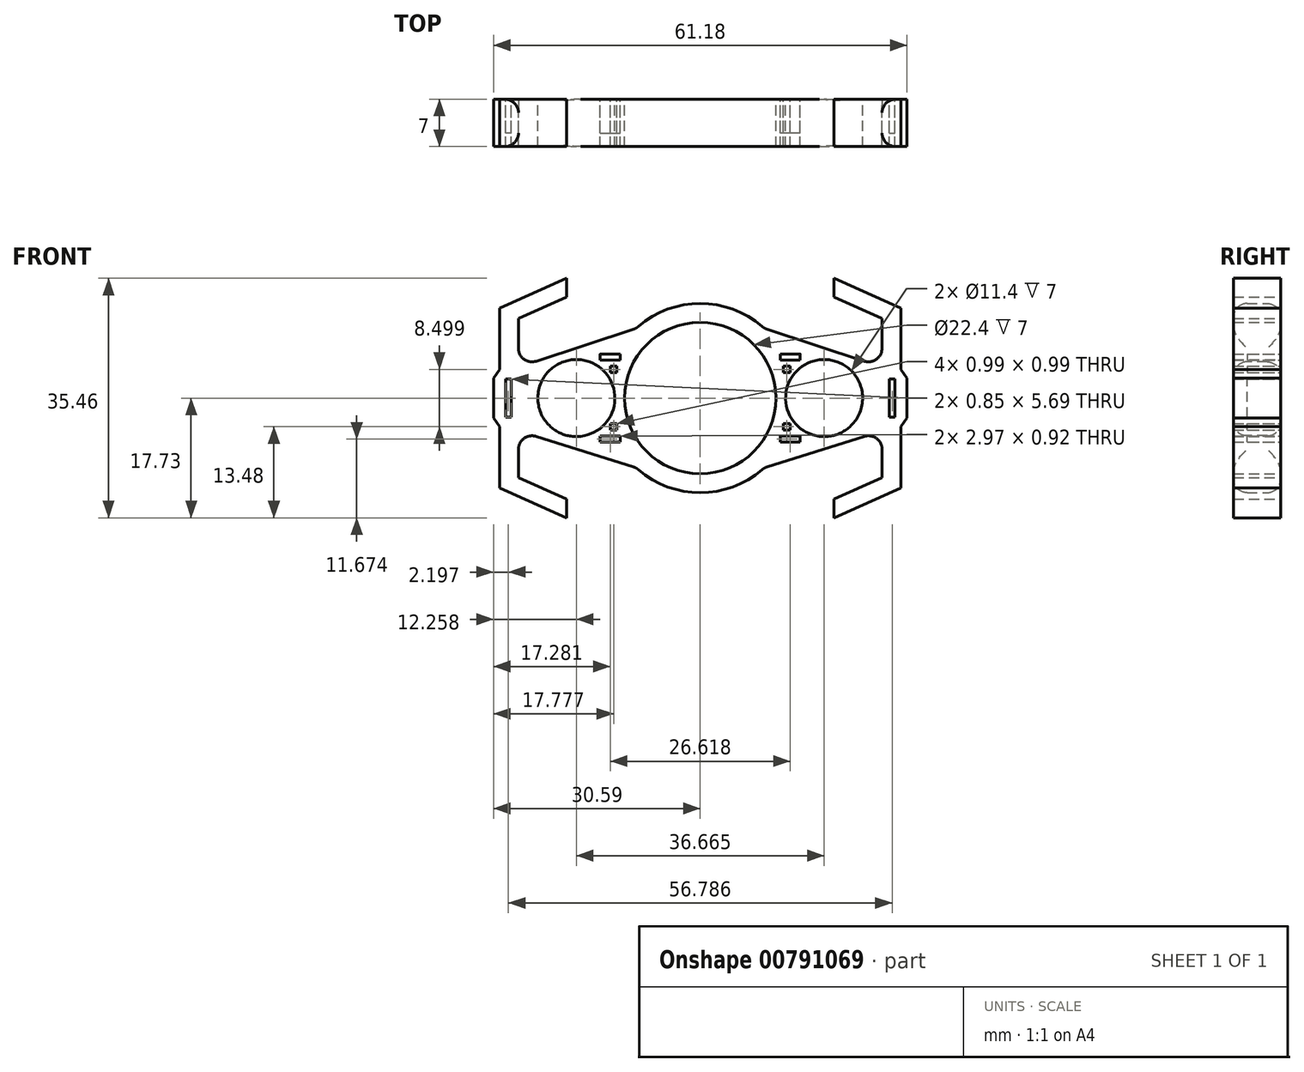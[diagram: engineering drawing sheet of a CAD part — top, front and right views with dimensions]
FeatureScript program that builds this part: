
annotation { "Feature Type Name" : "Feature", "Feature Type Description" : "" }
export const myFeature = defineFeature(function(context is Context, id is Id, definition is map)
    precondition{}
    {
        {
            var Q0;
            Q0=qCreatedBy(makeId("Front.planeOp"),FACE);
            var sketch = newSketch(context, id + "F0", { "sketchPlane" : qUnion([Q0])});
            skCircle(sketch, "E0", {"center": v(0, 0) * mm, "radius": 11.2 * mm});
            skArc(sketch, "E1", {"start": v(-9.46, -10.32) * mm, "mid": v(0, -14) * mm, "end": v(9.46, -10.32) * mm});
            skLineSegment(sketch, "E2", {"start": v(26.9, 4.6) * mm, "end": v(9.46, 10.32) * mm});
            skLineSegment(sketch, "E3", {"start": v(26.9, -4.86) * mm, "end": v(9.46, -10.32) * mm});
            skCircle(sketch, "E4", {"center": v(18.33, 0) * mm, "radius": 5.7 * mm});
            skLineSegment(sketch, "E5.right", {"start": v(29.7, 12.91) * mm, "end": v(29.7, 4.25) * mm});
            skPoint(sketch, "E6.orphan", {"position": v(0, 11.2) * mm});
            skLineSegment(sketch, "E7", {"start": v(29.7, -13.3) * mm, "end": v(19.79, -17.73) * mm});
            skLineSegment(sketch, "E8", {"start": v(19.79, -17.73) * mm, "end": v(19.79, -14.93) * mm});
            skLineSegment(sketch, "E9.top", {"start": v(29.7, -13.3) * mm, "end": v(29.69, -13.3) * mm});
            skLineSegment(sketch, "E9.left", {"start": v(29.7, 13.3) * mm, "end": v(29.7, 12.91) * mm});
            skLineSegment(sketch, "E10", {"start": v(19.79, -14.93) * mm, "end": v(26.9, -11.75) * mm});
            skLineSegment(sketch, "E11.MirrorCS", {"start": v(29.7, -13.3) * mm, "end": v(29.7, -12.91) * mm});
            skLineSegment(sketch, "E12.MirrorCS", {"start": v(29.7, 13.3) * mm, "end": v(19.79, 17.73) * mm});
            skLineSegment(sketch, "E13.MirrorCS", {"start": v(29.7, 13.3) * mm, "end": v(29.69, 13.3) * mm});
            skLineSegment(sketch, "E14.MirrorCS", {"start": v(19.79, 14.93) * mm, "end": v(26.9, 11.75) * mm});
            skLineSegment(sketch, "E15.MirrorCS", {"start": v(19.79, 17.73) * mm, "end": v(19.79, 14.93) * mm});
            skLineSegment(sketch, "E16.trimOffspring", {"start": v(26.9, 11.75) * mm, "end": v(26.9, 4.6) * mm});
            skLineSegment(sketch, "E17.trimOffspring", {"start": v(26.9, -11.75) * mm, "end": v(26.9, -4.86) * mm});
            skLineSegment(sketch, "E18.trimOffspring", {"start": v(29.7, 13.3) * mm, "end": v(29.7, 13.3) * mm});
            skLineSegment(sketch, "E19.trimOffspring", {"start": v(29.7, -13.3) * mm, "end": v(29.7, -13.3) * mm});
            skLineSegment(sketch, "E20", {"start": v(29.7, 4.25) * mm, "end": v(30.6, 2.96) * mm});
            skLineSegment(sketch, "E21", {"start": v(30.6, 2.96) * mm, "end": v(30.6, 0) * mm});
            skLineSegment(sketch, "E22.MirrorCS", {"start": v(30.6, -2.96) * mm, "end": v(30.6, 0) * mm});
            skLineSegment(sketch, "E23.MirrorCS", {"start": v(29.7, -4.25) * mm, "end": v(30.6, -2.96) * mm});
            skLineSegment(sketch, "E24.trimOffspring", {"start": v(29.7, -4.25) * mm, "end": v(29.7, -13.3) * mm});
            skLineSegment(sketch, "E25.MirrorCS", {"start": v(-29.7, -13.3) * mm, "end": v(-29.69, -13.3) * mm});
            skLineSegment(sketch, "E26.MirrorCS", {"start": v(-29.7, -13.3) * mm, "end": v(-29.7, -12.91) * mm});
            skLineSegment(sketch, "E27.MirrorCS", {"start": v(-29.7, -13.3) * mm, "end": v(-29.7, -13.3) * mm});
            skLineSegment(sketch, "E28.MirrorCS", {"start": v(-29.7, 13.3) * mm, "end": v(-29.7, 13.3) * mm});
            skLineSegment(sketch, "E29.MirrorCS", {"start": v(-29.7, 13.3) * mm, "end": v(-29.69, 13.3) * mm});
            skLineSegment(sketch, "E30.MirrorCS", {"start": v(-29.7, 13.3) * mm, "end": v(-29.7, 12.91) * mm});
            skLineSegment(sketch, "E31.MirrorCS", {"start": v(-19.79, -17.73) * mm, "end": v(-19.79, -14.93) * mm});
            skLineSegment(sketch, "E32.MirrorCS", {"start": v(-19.79, 17.73) * mm, "end": v(-19.79, 14.93) * mm});
            skLineSegment(sketch, "E33.MirrorCS", {"start": v(-30.6, 2.96) * mm, "end": v(-30.6, 0) * mm});
            skLineSegment(sketch, "E34.MirrorCS", {"start": v(-29.7, -4.25) * mm, "end": v(-30.6, -2.96) * mm});
            skLineSegment(sketch, "E35.MirrorCS", {"start": v(-29.7, 4.25) * mm, "end": v(-30.6, 2.96) * mm});
            skLineSegment(sketch, "E36.MirrorCS", {"start": v(-30.6, -2.96) * mm, "end": v(-30.6, 0) * mm});
            skLineSegment(sketch, "E37.MirrorCS", {"start": v(-29.7, 12.91) * mm, "end": v(-29.7, 4.25) * mm});
            skCircle(sketch, "E38.MirrorC", {"center": v(-18.33, 0) * mm, "radius": 5.7 * mm});
            skLineSegment(sketch, "E39.MirrorCS", {"start": v(-26.9, -11.75) * mm, "end": v(-26.9, -4.86) * mm});
            skLineSegment(sketch, "E40.MirrorCS", {"start": v(-29.7, 13.3) * mm, "end": v(-19.79, 17.73) * mm});
            skLineSegment(sketch, "E41.MirrorCS", {"start": v(-26.9, 11.75) * mm, "end": v(-26.9, 4.6) * mm});
            skLineSegment(sketch, "E42.MirrorCS", {"start": v(-29.7, -13.3) * mm, "end": v(-19.79, -17.73) * mm});
            skLineSegment(sketch, "E43.MirrorCS", {"start": v(-19.79, -14.93) * mm, "end": v(-26.9, -11.75) * mm});
            skLineSegment(sketch, "E44.MirrorCS", {"start": v(-29.7, -4.25) * mm, "end": v(-29.7, -13.3) * mm});
            skLineSegment(sketch, "E45.MirrorCS", {"start": v(-19.79, 14.93) * mm, "end": v(-26.9, 11.75) * mm});
            skLineSegment(sketch, "E46.MirrorCS", {"start": v(-26.9, 4.6) * mm, "end": v(-9.46, 10.32) * mm});
            skLineSegment(sketch, "E47.MirrorCS", {"start": v(-26.9, -4.86) * mm, "end": v(-9.46, -10.32) * mm});
            skArc(sketch, "E48.trimOffspring", {"start": v(9.46, 10.32) * mm, "mid": v(0, 14) * mm, "end": v(-9.46, 10.32) * mm});
            skLineSegment(sketch, "E49.bottom", {"start": v(-14.8, 6.52) * mm, "end": v(-11.82, 6.52) * mm});
            skLineSegment(sketch, "E49.top", {"start": v(-14.8, 5.6) * mm, "end": v(-11.82, 5.6) * mm});
            skLineSegment(sketch, "E49.left", {"start": v(-14.8, 6.52) * mm, "end": v(-14.8, 5.6) * mm});
            skLineSegment(sketch, "E49.right", {"start": v(-11.82, 6.52) * mm, "end": v(-11.82, 5.6) * mm});
            skLineSegment(sketch, "E50.bottom", {"start": v(-13.3, 4.75) * mm, "end": v(-12.32, 4.75) * mm});
            skLineSegment(sketch, "E50.top", {"start": v(-13.3, 3.75) * mm, "end": v(-12.32, 3.75) * mm});
            skLineSegment(sketch, "E50.left", {"start": v(-13.3, 4.75) * mm, "end": v(-13.3, 3.75) * mm});
            skLineSegment(sketch, "E50.right", {"start": v(-12.32, 4.75) * mm, "end": v(-12.32, 3.75) * mm});
            skLineSegment(sketch, "E51.bottom", {"start": v(-27.97, 2.85) * mm, "end": v(-28.82, 2.85) * mm});
            skLineSegment(sketch, "E51.left", {"start": v(-27.97, 2.85) * mm, "end": v(-27.97, 0) * mm});
            skLineSegment(sketch, "E51.right", {"start": v(-28.82, 2.85) * mm, "end": v(-28.82, 0) * mm});
            skLineSegment(sketch, "E52.MirrorCS", {"start": v(-28.82, -2.85) * mm, "end": v(-28.82, 0) * mm});
            skLineSegment(sketch, "E53.MirrorCS", {"start": v(-27.97, -2.85) * mm, "end": v(-27.97, 0) * mm});
            skLineSegment(sketch, "E54.MirrorCS", {"start": v(-27.97, -2.85) * mm, "end": v(-28.82, -2.85) * mm});
            skLineSegment(sketch, "E55.MirrorCS", {"start": v(-14.8, -6.52) * mm, "end": v(-14.8, -5.6) * mm});
            skLineSegment(sketch, "E56.MirrorCS", {"start": v(-14.8, -6.52) * mm, "end": v(-11.82, -6.52) * mm});
            skLineSegment(sketch, "E57.MirrorCS", {"start": v(-11.82, -6.52) * mm, "end": v(-11.82, -5.6) * mm});
            skLineSegment(sketch, "E58.MirrorCS", {"start": v(-14.8, -5.6) * mm, "end": v(-11.82, -5.6) * mm});
            skLineSegment(sketch, "E59.MirrorCS", {"start": v(-13.3, -4.75) * mm, "end": v(-12.32, -4.75) * mm});
            skLineSegment(sketch, "E60.MirrorCS", {"start": v(-12.32, -4.75) * mm, "end": v(-12.32, -3.75) * mm});
            skLineSegment(sketch, "E61.MirrorCS", {"start": v(-13.3, -4.75) * mm, "end": v(-13.3, -3.75) * mm});
            skLineSegment(sketch, "E62.MirrorCS", {"start": v(-13.3, -3.75) * mm, "end": v(-12.32, -3.75) * mm});
            skLineSegment(sketch, "E63.MirrorCS", {"start": v(14.8, 6.52) * mm, "end": v(11.82, 6.52) * mm});
            skLineSegment(sketch, "E64.MirrorCS", {"start": v(14.8, 5.6) * mm, "end": v(11.82, 5.6) * mm});
            skLineSegment(sketch, "E65.MirrorCS", {"start": v(11.82, 6.52) * mm, "end": v(11.82, 5.6) * mm});
            skLineSegment(sketch, "E66.MirrorCS", {"start": v(14.8, 6.52) * mm, "end": v(14.8, 5.6) * mm});
            skLineSegment(sketch, "E67.MirrorCS", {"start": v(13.3, 4.75) * mm, "end": v(13.3, 3.75) * mm});
            skLineSegment(sketch, "E68.MirrorCS", {"start": v(13.3, 4.75) * mm, "end": v(12.32, 4.75) * mm});
            skLineSegment(sketch, "E69.MirrorCS", {"start": v(12.32, 4.75) * mm, "end": v(12.32, 3.75) * mm});
            skLineSegment(sketch, "E70.MirrorCS", {"start": v(13.3, 3.75) * mm, "end": v(12.32, 3.75) * mm});
            skLineSegment(sketch, "E71.MirrorCS", {"start": v(13.3, -4.75) * mm, "end": v(12.32, -4.75) * mm});
            skLineSegment(sketch, "E72.MirrorCS", {"start": v(13.3, -4.75) * mm, "end": v(13.3, -3.75) * mm});
            skLineSegment(sketch, "E73.MirrorCS", {"start": v(13.3, -3.75) * mm, "end": v(12.32, -3.75) * mm});
            skLineSegment(sketch, "E74.MirrorCS", {"start": v(12.32, -4.75) * mm, "end": v(12.32, -3.75) * mm});
            skLineSegment(sketch, "E75.MirrorCS", {"start": v(14.8, -5.6) * mm, "end": v(11.82, -5.6) * mm});
            skLineSegment(sketch, "E76.MirrorCS", {"start": v(11.82, -6.52) * mm, "end": v(11.82, -5.6) * mm});
            skLineSegment(sketch, "E77.MirrorCS", {"start": v(14.8, -6.52) * mm, "end": v(11.82, -6.52) * mm});
            skLineSegment(sketch, "E78.MirrorCS", {"start": v(14.8, -6.52) * mm, "end": v(14.8, -5.6) * mm});
            skLineSegment(sketch, "E79.MirrorCS", {"start": v(28.82, -2.85) * mm, "end": v(28.82, 0) * mm});
            skLineSegment(sketch, "E80.MirrorCS", {"start": v(27.97, -2.85) * mm, "end": v(27.97, 0) * mm});
            skLineSegment(sketch, "E81.MirrorCS", {"start": v(27.97, -2.85) * mm, "end": v(28.82, -2.85) * mm});
            skLineSegment(sketch, "E82.MirrorCS", {"start": v(27.97, 2.85) * mm, "end": v(28.82, 2.85) * mm});
            skLineSegment(sketch, "E83.MirrorCS", {"start": v(27.97, 2.85) * mm, "end": v(27.97, 0) * mm});
            skLineSegment(sketch, "E84.MirrorCS", {"start": v(28.82, 2.85) * mm, "end": v(28.82, 0) * mm});
            skSolve(sketch);
        }
        {
            var Q0;
            Q0=makeQuery(id+"F0.imprint","IMPRINT",FACE,{"disambiguationData":[TD([[makeQuery(id+"F0.imprint","IMPRINT",EDGE,{"derivedFrom":sQuery(id+"F0.wireOp",EDGE,"E63.MirrorCS")}),1.0]])]});
            var Q1;
            Q1=makeQuery(id+"F0.imprint","IMPRINT",FACE,{"disambiguationData":[TD([[makeQuery(id+"F0.imprint","IMPRINT",EDGE,{"derivedFrom":sQuery(id+"F0.wireOp",EDGE,"E67.MirrorCS")}),-1.0]])]});
            var Q2;
            Q2=makeQuery(id+"F0.imprint","IMPRINT",FACE,{"disambiguationData":[TD([[makeQuery(id+"F0.imprint","IMPRINT",EDGE,{"derivedFrom":sQuery(id+"F0.wireOp",EDGE,"E71.MirrorCS")}),-1.0]])]});
            var Q3;
            Q3=makeQuery(id+"F0.imprint","IMPRINT",FACE,{"disambiguationData":[TD([[makeQuery(id+"F0.imprint","IMPRINT",EDGE,{"derivedFrom":sQuery(id+"F0.wireOp",EDGE,"E75.MirrorCS")}),1.0]])]});
            var Q4;
            Q4=makeQuery(id+"F0.imprint","IMPRINT",FACE,{"disambiguationData":[TD([[makeQuery(id+"F0.imprint","IMPRINT",EDGE,{"derivedFrom":sQuery(id+"F0.wireOp",EDGE,"E79.MirrorCS")}),1.0]])]});
            var Q5;
            Q5=makeQuery(id+"F0.imprint","IMPRINT",FACE,{"disambiguationData":[TD([[makeQuery(id+"F0.imprint","IMPRINT",EDGE,{"derivedFrom":sQuery(id+"F0.wireOp",EDGE,"E57.MirrorCS")}),1.0]])]});
            var Q6;
            Q6=makeQuery(id+"F0.imprint","IMPRINT",FACE,{"disambiguationData":[TD([[makeQuery(id+"F0.imprint","IMPRINT",EDGE,{"derivedFrom":sQuery(id+"F0.wireOp",EDGE,"E60.MirrorCS")}),1.0]])]});
            var Q7;
            Q7=makeQuery(id+"F0.imprint","IMPRINT",FACE,{"disambiguationData":[TD([[makeQuery(id+"F0.imprint","IMPRINT",EDGE,{"derivedFrom":sQuery(id+"F0.wireOp",EDGE,"E50.bottom")}),-1.0]])]});
            var Q8;
            Q8=makeQuery(id+"F0.imprint","IMPRINT",FACE,{"disambiguationData":[TD([[makeQuery(id+"F0.imprint","IMPRINT",EDGE,{"derivedFrom":sQuery(id+"F0.wireOp",EDGE,"E49.bottom")}),-1.0]])]});
            var Q9;
            Q9=makeQuery(id+"F0.imprint","IMPRINT",FACE,{"disambiguationData":[TD([[makeQuery(id+"F0.imprint","IMPRINT",EDGE,{"derivedFrom":sQuery(id+"F0.wireOp",EDGE,"E51.bottom")}),1.0]])]});
            extrude(context, id + "F1", {"entities" : qUnion([Q0, Q1, Q2, Q3, Q4, Q5, Q6, Q7, Q8, Q9]), "depth" : 5 * mm, "offsetDistance" : 25 * mm});
        }
        {
            var Q0;
            Q0=makeQuery(id+"F0.imprint","IMPRINT",FACE,{"disambiguationData":[TD([[makeQuery(id+"F0.imprint","IMPRINT",EDGE,{"derivedFrom":sQuery(id+"F0.wireOp",EDGE,"E0")}),-1.0]])]});
            extrude(context, id + "F2", {"entities" : qUnion([Q0]), "depth" : 7 * mm, "offsetDistance" : 25 * mm});
        }
        {
            var Q0;
            Q0=makeQuery(id+"F2.opExtrude","SWEPT_FACE",FACE,{"disambiguationData":[OSD([sQuery(id+"F0.wireOp",EDGE,"E1")])]});
            var Q1;
            Q1=makeQuery(id+"F2.opExtrude","SWEPT_FACE",FACE,{"disambiguationData":[OSD([sQuery(id+"F0.wireOp",EDGE,"E47.MirrorCS")])]});
            var Q2;
            Q2=makeQuery(id+"F2.opExtrude","SWEPT_FACE",FACE,{"disambiguationData":[OSD([sQuery(id+"F0.wireOp",EDGE,"E3")])]});
            var Q3;
            Q3=makeQuery(id+"F2.opExtrude","SWEPT_FACE",FACE,{"disambiguationData":[OSD([sQuery(id+"F0.wireOp",EDGE,"E2")])]});
            var Q4;
            Q4=makeQuery(id+"F2.opExtrude","SWEPT_FACE",FACE,{"disambiguationData":[OSD([sQuery(id+"F0.wireOp",EDGE,"E48.trimOffspring")])]});
            var Q5;
            Q5=makeQuery(id+"F2.opExtrude","SWEPT_FACE",FACE,{"disambiguationData":[OSD([sQuery(id+"F0.wireOp",EDGE,"E46.MirrorCS")])]});
            fillet(context, id + "F3", {"entities" : qUnion([Q0, Q1, Q2, Q3, Q4, Q5]), "radius" : 2 * mm, "tangentPropagation" : true, "allowEdgeOverflow" : false});
        }
    });
